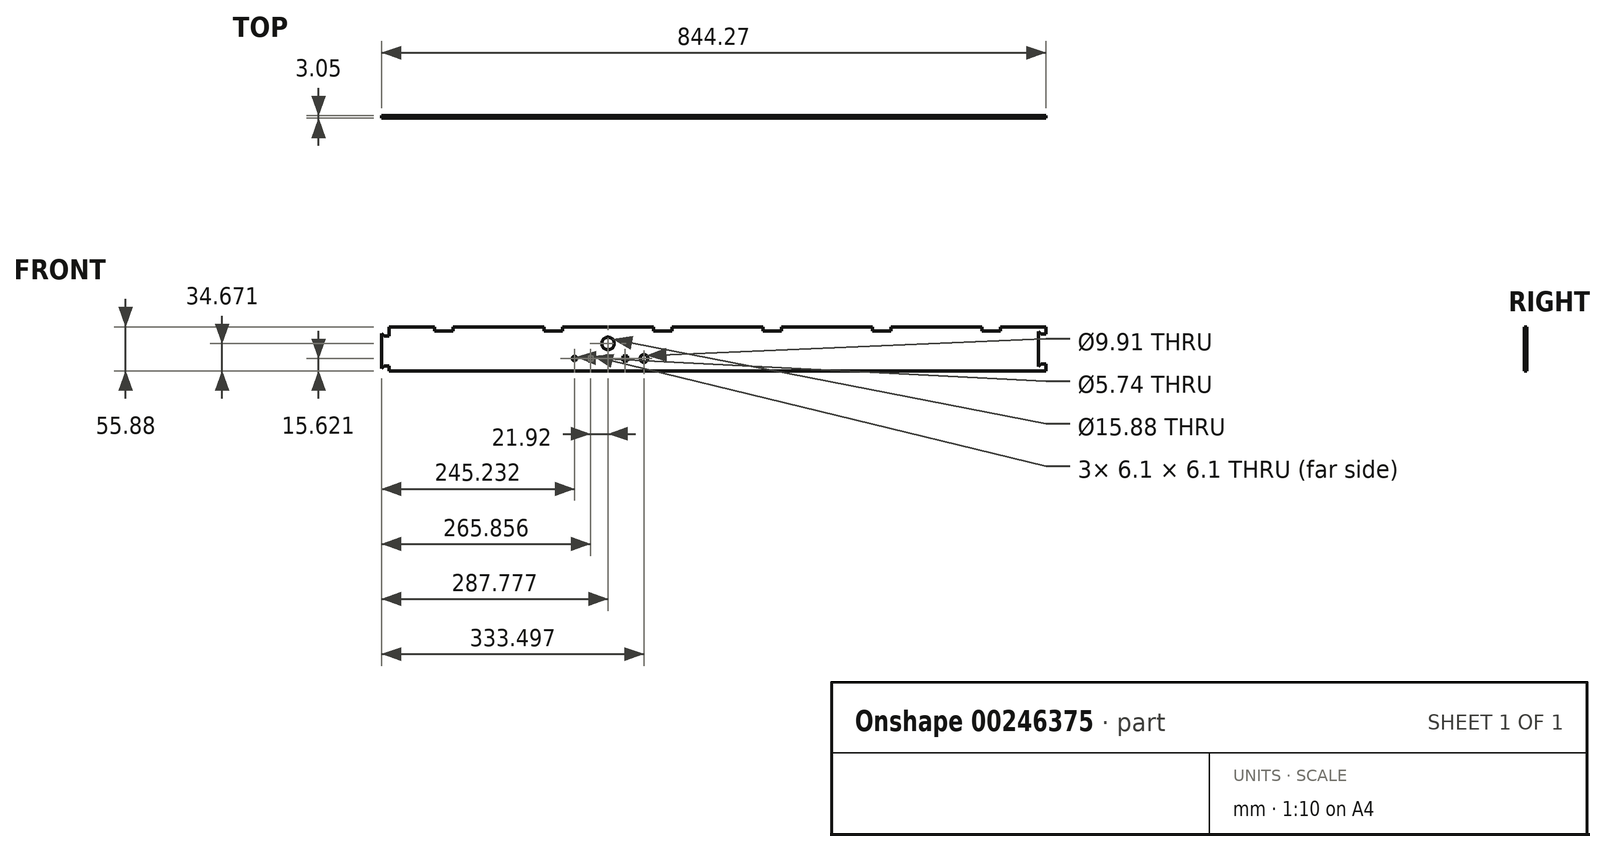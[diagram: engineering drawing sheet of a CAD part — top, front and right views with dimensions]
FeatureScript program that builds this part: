
annotation { "Feature Type Name" : "Feature", "Feature Type Description" : "" }
export const myFeature = defineFeature(function(context is Context, id is Id, definition is map)
    precondition{}
    {
        {
            var Q0;
            Q0=qCreatedBy(makeId("Front.planeOp"),FACE);
            var sketch = newSketch(context, id + "F0", { "sketchPlane" : qUnion([Q0])});
            skLineSegment(sketch, "E0.bottom", {"start": v(0, 0) * mm, "end": v(834.74, 0) * mm});
            skLineSegment(sketch, "E0.top", {"start": v(0, 50.8) * mm, "end": v(834.74, 50.8) * mm});
            skLineSegment(sketch, "E0.left", {"start": v(0, 0) * mm, "end": v(0, 50.8) * mm});
            skLineSegment(sketch, "E0.right", {"start": v(834.74, 0) * mm, "end": v(834.74, 50.8) * mm});
            skLineSegment(sketch, "E1", {"start": v(57.92, 50.8) * mm, "end": v(57.92, 0) * mm, "construction": true});
            skLineSegment(sketch, "E2", {"start": v(75.88, 50.8) * mm, "end": v(75.88, 0) * mm, "construction": true});
            skLineSegment(sketch, "E3", {"start": v(776.82, 50.8) * mm, "end": v(776.82, 0) * mm, "construction": true});
            skLineSegment(sketch, "E4", {"start": v(758.86, 50.8) * mm, "end": v(758.86, 0) * mm, "construction": true});
            skSolve(sketch);
        }
        {
            var Q0;
            Q0=makeQuery(id+"F0.imprint","IMPRINT",FACE,{"disambiguationData":[TD([[makeQuery(id+"F0.imprint","IMPRINT",EDGE,{"derivedFrom":sQuery(id+"F0.wireOp",EDGE,"E0.bottom")}),1.0]])]});
            extrude(context, id + "F1", {"entities" : qUnion([Q0]), "depth" : 3.05 * mm});
        }
        {
            var Q0;
            Q0=makeQuery(id+"F1.opExtrude","CAP_FACE",FACE,{"disambiguationData":[OSD([sQuery(id+"F0.wireOp",EDGE,"E0.bottom"),sQuery(id+"F0.wireOp",EDGE,"E0.top"),sQuery(id+"F0.wireOp",EDGE,"E0.left"),sQuery(id+"F0.wireOp",EDGE,"E0.right")])],"isStart":false});
            var sketch = newSketch(context, id + "F2", { "sketchPlane" : qUnion([Q0])});
            skLineSegment(sketch, "E5", {"start": v(57.92, 0) * mm, "end": v(57.92, 50.8) * mm});
            skLineSegment(sketch, "E6", {"start": v(81.2, 0) * mm, "end": v(81.2, 50.8) * mm});
            skLineSegment(sketch, "E7", {"start": v(776.82, 0) * mm, "end": v(776.82, 50.8) * mm});
            skLineSegment(sketch, "E8", {"start": v(753.54, 0) * mm, "end": v(753.54, 50.8) * mm});
            skLineSegment(sketch, "E9", {"start": v(197.05, 50.8) * mm, "end": v(197.05, 0) * mm});
            skLineSegment(sketch, "E10", {"start": v(220.32, 0) * mm, "end": v(220.32, 50.8) * mm});
            skLineSegment(sketch, "E11", {"start": v(336.17, 50.8) * mm, "end": v(336.17, 0) * mm});
            skLineSegment(sketch, "E12", {"start": v(359.45, 0.94) * mm, "end": v(359.45, 50.8) * mm});
            skLineSegment(sketch, "E13", {"start": v(475.3, 0) * mm, "end": v(475.3, 50.8) * mm});
            skLineSegment(sketch, "E14", {"start": v(498.57, 0) * mm, "end": v(498.57, 50.8) * mm});
            skLineSegment(sketch, "E15", {"start": v(614.42, 50.8) * mm, "end": v(614.42, 0) * mm});
            skLineSegment(sketch, "E16", {"start": v(637.7, 50.8) * mm, "end": v(637.7, 0) * mm});
            skCircle(sketch, "E17", {"center": v(9.53, 25.4) * mm, "radius": 1.27 * mm});
            skPoint(sketch, "E17.centerSnap0", {"position": v(0, 25.4) * mm});
            skCircle(sketch, "E18", {"center": v(825.22, 25.4) * mm, "radius": 1.27 * mm});
            skSolve(sketch);
        }
        {
            var Q0;
            {var subQ0=sQuery(id+"F2.wireOp",EDGE,"E6");Q0=makeQuery(id+"F2.imprint","IMPRINT",FACE,{"disambiguationData":[TD([[makeQuery(id+"F2.imprint","IMPRINT",EDGE,{"derivedFrom":subQ0}),-1.0]])]});}
            var sketch = newSketch(context, id + "F3", { "sketchPlane" : qUnion([Q0])});
            skLineSegment(sketch, "E19", {"start": v(0, 25.4) * mm, "end": v(834.74, 25.4) * mm, "construction": true});
            skLineSegment(sketch, "E20", {"start": v(0, 50.8) * mm, "end": v(0, 55.88) * mm});
            skLineSegment(sketch, "E21", {"start": v(0, 55.88) * mm, "end": v(57.92, 55.88) * mm});
            skLineSegment(sketch, "E22", {"start": v(57.92, 55.88) * mm, "end": v(57.92, 50.8) * mm});
            skLineSegment(sketch, "E23", {"start": v(81.2, 50.8) * mm, "end": v(81.2, 55.88) * mm});
            skLineSegment(sketch, "E24", {"start": v(81.2, 55.88) * mm, "end": v(197.05, 55.88) * mm});
            skLineSegment(sketch, "E25", {"start": v(197.05, 55.88) * mm, "end": v(197.05, 50.8) * mm});
            skLineSegment(sketch, "E26", {"start": v(220.32, 50.8) * mm, "end": v(220.32, 55.88) * mm});
            skLineSegment(sketch, "E27", {"start": v(220.32, 55.88) * mm, "end": v(336.17, 55.88) * mm});
            skLineSegment(sketch, "E28", {"start": v(336.17, 55.88) * mm, "end": v(336.17, 50.8) * mm});
            skLineSegment(sketch, "E29", {"start": v(359.45, 50.8) * mm, "end": v(359.45, 55.88) * mm});
            skLineSegment(sketch, "E30", {"start": v(359.45, 55.88) * mm, "end": v(475.3, 55.88) * mm});
            skLineSegment(sketch, "E31", {"start": v(475.3, 55.88) * mm, "end": v(475.3, 50.8) * mm});
            skLineSegment(sketch, "E32", {"start": v(498.57, 50.8) * mm, "end": v(498.57, 55.88) * mm});
            skLineSegment(sketch, "E33", {"start": v(498.57, 55.88) * mm, "end": v(614.42, 55.88) * mm});
            skLineSegment(sketch, "E34", {"start": v(614.42, 55.88) * mm, "end": v(614.42, 50.8) * mm});
            skLineSegment(sketch, "E35", {"start": v(637.7, 50.8) * mm, "end": v(637.7, 55.88) * mm});
            skLineSegment(sketch, "E36", {"start": v(637.7, 55.88) * mm, "end": v(753.54, 55.88) * mm});
            skLineSegment(sketch, "E37", {"start": v(753.54, 55.88) * mm, "end": v(753.54, 50.8) * mm});
            skLineSegment(sketch, "E38", {"start": v(776.82, 50.8) * mm, "end": v(776.82, 55.88) * mm});
            skLineSegment(sketch, "E39", {"start": v(776.82, 55.88) * mm, "end": v(834.74, 55.88) * mm});
            skLineSegment(sketch, "E40", {"start": v(834.74, 55.88) * mm, "end": v(834.74, 50.8) * mm});
            skLineSegment(sketch, "E41", {"start": v(0, 50.8) * mm, "end": v(834.74, 50.8) * mm});
            skLineSegment(sketch, "E42", {"start": v(834.74, 0) * mm, "end": v(0, 0) * mm});
            skSolve(sketch);
        }
        {
            var Q0;
            {var subQ0=sQuery(id+"F3.wireOp",EDGE,"E20");Q0=makeQuery(id+"F3.imprint","IMPRINT",FACE,{"disambiguationData":[TD([[makeQuery(id+"F3.imprint","IMPRINT",EDGE,{"derivedFrom":subQ0}),-1.0]])]});}
            var Q1;
            {var subQ0=sQuery(id+"F3.wireOp",EDGE,"E23");Q1=makeQuery(id+"F3.imprint","IMPRINT",FACE,{"disambiguationData":[TD([[makeQuery(id+"F3.imprint","IMPRINT",EDGE,{"derivedFrom":subQ0}),-1.0]])]});}
            var Q2;
            {var subQ0=sQuery(id+"F3.wireOp",EDGE,"300d203a-4e24-4113-8f0b-c0bd62af7ee03.MirrorCS");Q2=makeQuery(id+"F3.imprint","IMPRINT",FACE,{"disambiguationData":[TD([[makeQuery(id+"F3.imprint","IMPRINT",EDGE,{"derivedFrom":subQ0}),1.0]])]});}
            var Q3;
            {var subQ0=sQuery(id+"F3.wireOp",EDGE,"300d203a-4e24-4113-8f0b-c0bd62af7ee06.MirrorCS");Q3=makeQuery(id+"F3.imprint","IMPRINT",FACE,{"disambiguationData":[TD([[makeQuery(id+"F3.imprint","IMPRINT",EDGE,{"derivedFrom":subQ0}),1.0]])]});}
            var Q4;
            {var subQ0=sQuery(id+"F3.wireOp",EDGE,"E26");Q4=makeQuery(id+"F3.imprint","IMPRINT",FACE,{"disambiguationData":[TD([[makeQuery(id+"F3.imprint","IMPRINT",EDGE,{"derivedFrom":subQ0}),-1.0]])]});}
            var Q5;
            {var subQ0=sQuery(id+"F3.wireOp",EDGE,"300d203a-4e24-4113-8f0b-c0bd62af7ee09.MirrorCS");Q5=makeQuery(id+"F3.imprint","IMPRINT",FACE,{"disambiguationData":[TD([[makeQuery(id+"F3.imprint","IMPRINT",EDGE,{"derivedFrom":subQ0}),1.0]])]});}
            var Q6;
            {var subQ0=sQuery(id+"F3.wireOp",EDGE,"E29");Q6=makeQuery(id+"F3.imprint","IMPRINT",FACE,{"disambiguationData":[TD([[makeQuery(id+"F3.imprint","IMPRINT",EDGE,{"derivedFrom":subQ0}),-1.0]])]});}
            var Q7;
            {var subQ0=sQuery(id+"F3.wireOp",EDGE,"300d203a-4e24-4113-8f0b-c0bd62af7ee05.MirrorCS");Q7=makeQuery(id+"F3.imprint","IMPRINT",FACE,{"disambiguationData":[TD([[makeQuery(id+"F3.imprint","IMPRINT",EDGE,{"derivedFrom":subQ0}),1.0]])]});}
            var Q8;
            {var subQ0=sQuery(id+"F3.wireOp",EDGE,"E32");Q8=makeQuery(id+"F3.imprint","IMPRINT",FACE,{"disambiguationData":[TD([[makeQuery(id+"F3.imprint","IMPRINT",EDGE,{"derivedFrom":subQ0}),-1.0]])]});}
            var Q9;
            {var subQ0=sQuery(id+"F3.wireOp",EDGE,"300d203a-4e24-4113-8f0b-c0bd62af7ee02.MirrorCS");Q9=makeQuery(id+"F3.imprint","IMPRINT",FACE,{"disambiguationData":[TD([[makeQuery(id+"F3.imprint","IMPRINT",EDGE,{"derivedFrom":subQ0}),1.0]])]});}
            var Q10;
            {var subQ0=sQuery(id+"F3.wireOp",EDGE,"E35");Q10=makeQuery(id+"F3.imprint","IMPRINT",FACE,{"disambiguationData":[TD([[makeQuery(id+"F3.imprint","IMPRINT",EDGE,{"derivedFrom":subQ0}),-1.0]])]});}
            var Q11;
            {var subQ0=sQuery(id+"F3.wireOp",EDGE,"300d203a-4e24-4113-8f0b-c0bd62af7ee00.MirrorCS");Q11=makeQuery(id+"F3.imprint","IMPRINT",FACE,{"disambiguationData":[TD([[makeQuery(id+"F3.imprint","IMPRINT",EDGE,{"derivedFrom":subQ0}),1.0]])]});}
            var Q12;
            {var subQ0=sQuery(id+"F3.wireOp",EDGE,"E38");Q12=makeQuery(id+"F3.imprint","IMPRINT",FACE,{"disambiguationData":[TD([[makeQuery(id+"F3.imprint","IMPRINT",EDGE,{"derivedFrom":subQ0}),-1.0]])]});}
            var Q13;
            {var subQ0=sQuery(id+"F3.wireOp",EDGE,"300d203a-4e24-4113-8f0b-c0bd62af7ee04.MirrorCS");Q13=makeQuery(id+"F3.imprint","IMPRINT",FACE,{"disambiguationData":[TD([[makeQuery(id+"F3.imprint","IMPRINT",EDGE,{"derivedFrom":subQ0}),1.0]])]});}
            extrude(context, id + "F4", {"entities" : qUnion([Q0, Q1, Q2, Q3, Q4, Q5, Q6, Q7, Q8, Q9, Q10, Q11, Q12, Q13]), "operationType" : NewBodyOperationType.ADD, "oppositeDirection" : true, "depth" : 3.05 * mm});
        }
        {
            var Q0;
            {var subQ0=sQuery(id+"F2.wireOp",EDGE,"E6");Q0=makeQuery(id+"F2.imprint","IMPRINT",FACE,{"disambiguationData":[TD([[makeQuery(id+"F2.imprint","IMPRINT",EDGE,{"derivedFrom":subQ0}),-1.0]])]});}
            var sketch = newSketch(context, id + "F5", { "sketchPlane" : qUnion([Q0])});
            skLineSegment(sketch, "E43", {"start": v(0, 6.35) * mm, "end": v(0, 44.45) * mm});
            skPoint(sketch, "E44", {"position": v(0, 25.4) * mm});
            skLineSegment(sketch, "E45", {"start": v(0, 44.45) * mm, "end": v(-6.35, 44.45) * mm});
            skLineSegment(sketch, "E46", {"start": v(0, 6.35) * mm, "end": v(-6.35, 6.35) * mm});
            skLineSegment(sketch, "E47", {"start": v(-6.35, 44.45) * mm, "end": v(-9.52, 47.63) * mm});
            skLineSegment(sketch, "E48", {"start": v(-6.35, 6.35) * mm, "end": v(-9.52, 3.18) * mm});
            skLineSegment(sketch, "E49", {"start": v(-9.52, 47.63) * mm, "end": v(-9.52, 3.18) * mm});
            skLineSegment(sketch, "E50", {"start": v(834.74, 8.9) * mm, "end": v(834.74, 47) * mm});
            skPoint(sketch, "E51", {"position": v(834.74, 27.94) * mm});
            skLineSegment(sketch, "E52", {"start": v(834.74, 47) * mm, "end": v(828.4, 47) * mm});
            skLineSegment(sketch, "E53", {"start": v(834.74, 8.9) * mm, "end": v(828.4, 8.9) * mm});
            skLineSegment(sketch, "E54", {"start": v(828.4, 47) * mm, "end": v(825.22, 50.17) * mm});
            skLineSegment(sketch, "E55", {"start": v(828.4, 8.9) * mm, "end": v(825.22, 5.72) * mm});
            skLineSegment(sketch, "E56", {"start": v(825.22, 50.17) * mm, "end": v(825.22, 5.72) * mm});
            skSolve(sketch);
        }
        {
            var Q0;
            Q0=makeQuery(id+"F5.imprint","IMPRINT",FACE,{"disambiguationData":[TD([[makeQuery(id+"F5.imprint","IMPRINT",EDGE,{"derivedFrom":sQuery(id+"F5.wireOp",EDGE,"E43")}),1.0]])]});
            extrude(context, id + "F6", {"entities" : qUnion([Q0]), "operationType" : NewBodyOperationType.ADD, "oppositeDirection" : true, "depth" : 3.05 * mm});
        }
        {
            var Q0;
            Q0=makeQuery(id+"F5.imprint","IMPRINT",FACE,{"disambiguationData":[TD([[makeQuery(id+"F5.imprint","IMPRINT",EDGE,{"derivedFrom":sQuery(id+"F5.wireOp",EDGE,"E50")}),1.0]])]});
            extrude(context, id + "F7", {"entities" : qUnion([Q0]), "operationType" : NewBodyOperationType.REMOVE, "endBound" : BoundingType.THROUGH_ALL, "oppositeDirection" : true, "depth" : 25.4 * mm});
        }
        {
            var Q0;
            {var subQ0=sQuery(id+"F2.wireOp",EDGE,"E10");Q0=makeQuery(id+"F2.imprint","IMPRINT",FACE,{"disambiguationData":[TD([[makeQuery(id+"F2.imprint","IMPRINT",EDGE,{"derivedFrom":subQ0}),-1.0]])]});}
            var sketch = newSketch(context, id + "F8", { "sketchPlane" : qUnion([Q0])});
            skLineSegment(sketch, "E57.bottom", {"start": v(245.23, 21.59) * mm, "end": v(311.27, 21.59) * mm, "construction": true});
            skLineSegment(sketch, "E57.top", {"start": v(245.23, 9.65) * mm, "end": v(311.27, 9.65) * mm, "construction": true});
            skLineSegment(sketch, "E57.left", {"start": v(245.23, 21.59) * mm, "end": v(245.23, 9.65) * mm, "construction": true});
            skLineSegment(sketch, "E57.right", {"start": v(311.27, 21.59) * mm, "end": v(311.27, 9.65) * mm, "construction": true});
            skPoint(sketch, "E58", {"position": v(278.25, 9.65) * mm});
            skLineSegment(sketch, "E59.bottom", {"start": v(253.28, 12.57) * mm, "end": v(259.37, 12.57) * mm});
            skLineSegment(sketch, "E59.top", {"start": v(253.28, 18.67) * mm, "end": v(259.37, 18.67) * mm});
            skLineSegment(sketch, "E59.left", {"start": v(253.28, 12.57) * mm, "end": v(253.28, 18.67) * mm});
            skLineSegment(sketch, "E59.right", {"start": v(259.37, 12.57) * mm, "end": v(259.37, 18.67) * mm});
            skLineSegment(sketch, "E60.bottom", {"start": v(275.2, 12.57) * mm, "end": v(281.3, 12.57) * mm});
            skLineSegment(sketch, "E60.top", {"start": v(275.2, 18.67) * mm, "end": v(281.3, 18.67) * mm});
            skLineSegment(sketch, "E60.left", {"start": v(275.2, 12.57) * mm, "end": v(275.2, 18.67) * mm});
            skLineSegment(sketch, "E60.right", {"start": v(281.3, 12.57) * mm, "end": v(281.3, 18.67) * mm});
            skLineSegment(sketch, "E61.bottom", {"start": v(297.12, 12.57) * mm, "end": v(303.21, 12.57) * mm});
            skLineSegment(sketch, "E61.top", {"start": v(297.12, 18.67) * mm, "end": v(303.21, 18.67) * mm});
            skLineSegment(sketch, "E61.left", {"start": v(297.12, 12.57) * mm, "end": v(297.12, 18.67) * mm});
            skLineSegment(sketch, "E61.right", {"start": v(303.21, 12.57) * mm, "end": v(303.21, 18.67) * mm});
            skPoint(sketch, "E62", {"position": v(253.28, 15.62) * mm});
            skPoint(sketch, "E63", {"position": v(245.23, 15.62) * mm});
            skPoint(sketch, "E64", {"position": v(278.25, 18.67) * mm});
            skPoint(sketch, "E65", {"position": v(275.2, 15.62) * mm});
            skPoint(sketch, "E66", {"position": v(297.12, 15.62) * mm});
            skPoint(sketch, "E67", {"position": v(300.17, 18.67) * mm});
            skCircle(sketch, "E68", {"center": v(235.7, 15.62) * mm, "radius": 2.87 * mm});
            skCircle(sketch, "E69", {"center": v(323.97, 15.62) * mm, "radius": 4.95 * mm});
            skCircle(sketch, "E70", {"center": v(278.25, 34.67) * mm, "radius": 7.94 * mm});
            skSolve(sketch);
        }
        {
            var Q0;
            Q0 = qSketchRegion(id + "F8", true);
            extrude(context, id + "F9", {"entities" : qUnion([Q0]), "operationType" : NewBodyOperationType.REMOVE, "endBound" : BoundingType.THROUGH_ALL, "oppositeDirection" : true, "depth" : 25.4 * mm});
        }
    });
